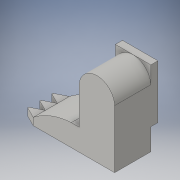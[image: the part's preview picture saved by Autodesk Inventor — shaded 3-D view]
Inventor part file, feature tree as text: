
AUTODESK INVENTOR PART (.ipt)
format: ipt  version: 2016 (Build 200138000, 138)  size: 201,728 bytes
history: native  units: in
note: dims shown in document units (in); Inventor stores cm internally (conversion verified against a paired STEP export)
features: extrude x9, sketch x9, reference x9, plane x1, fillet x1
ambient origin geometry x8: Origin, YZ Plane, XZ Plane, XY Plane, X Axis, Y Axis, Z Axis, Center Point
bodies: Solid1 (feature_tree)
feature tree (29):
  extrude  "Extrusion1"  Depth=0.0098in
  extrude  "Extrusion2"  Depth=0.0098in
  extrude  "Extrusion3"  Depth=0.1969in
  extrude  "Extrusion5"  Depth=0.6in
  extrude  "Extrusion6"  Depth=1.0in TaperAngle=0.0deg
  plane  "Work Plane1"
  extrude  "Extrusion7"  Depth=0.2in TaperAngle=0.0deg
  extrude  "Extrusion8"  [1 undecoded]
  extrude  "Extrusion9"  Depth=0.0394in
  extrude  "Extrusion10"  Depth=0.2362in TaperAngle=0.0deg
  fillet  "Fillet1"  Radius=0.5in
  sketch  "Sketch1"  dims[d0=0.0098in d1=0.0098in]
  reference  "Reference1"
  reference  "Reference2"
  reference  "Reference3"
  reference  "Reference4"
  reference  "Reference5"
  sketch  "Sketch2"  dims[d2=0.0098in d3=0.0098in]
  sketch  "Sketch3"  dims[d4=0.1969in d5=0.0in d6=0.98in]
  reference  "Reference6"
  sketch  "Sketch5"  dims[d7=1.0in d8=0.0in d9=0.6in]
  sketch  "Sketch6"  dims[d10=2.25in d12=1.0in d13=0.0in]
  sketch  "Sketch7"  dims[d16=0.3333in d22=0.2in d23=0.0in]
  reference  "Reference7"
  sketch  "Sketch8"  dims[d24=100.0in d25=0.0in d26=-0.5in]
  reference  "Reference8"
  sketch  "Sketch9"  dims[d27=0.0394in d28=0.0394in]
  sketch  "Sketch10"  dims[d29=0.0394in d30=0.2362in d31=0.0in d32=0.5in d33=0.0in d34=0.1378in d35=0.1969in d36=0.1969in d37=0.1211in d38=0.1211in d39=0.1969in d40=0.0in d41=0.1969in d42=0.0in d43=0.0197in]
  reference  "Reference9"
note: 1 required parameter value undecoded (feature->parameter linkage not recoverable at this tier; creation-order binding heuristic only, values carry confidence <= 0.55)
